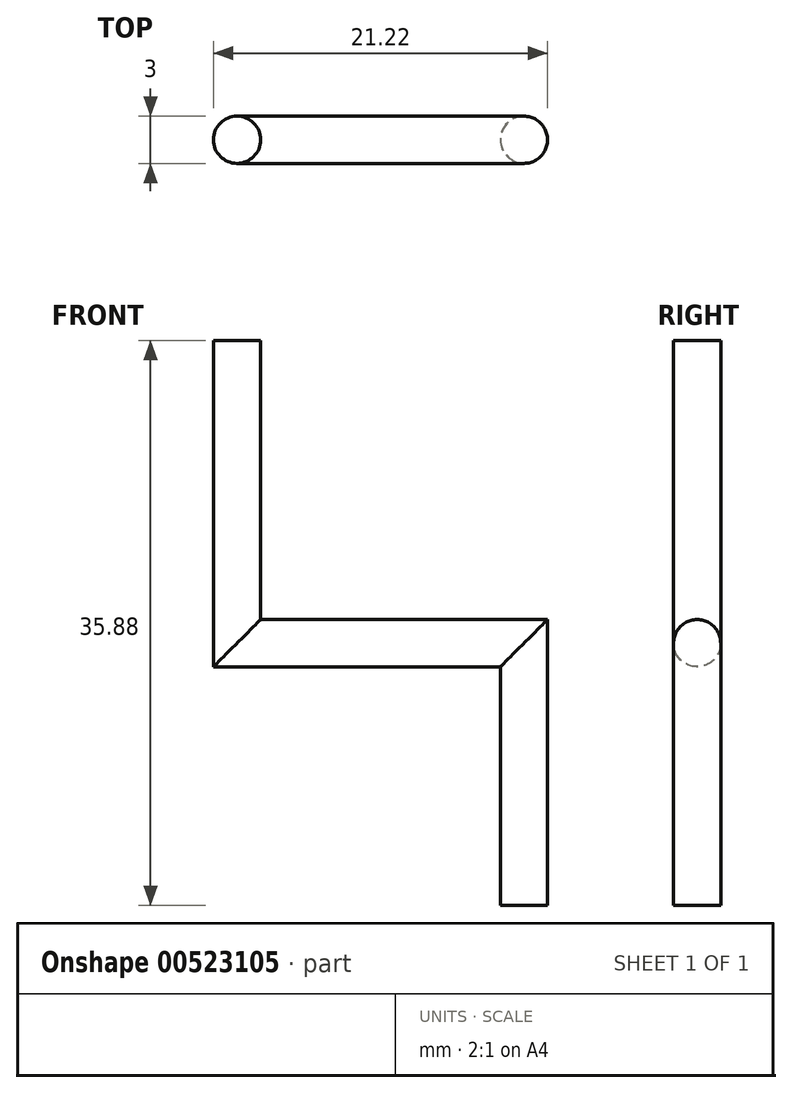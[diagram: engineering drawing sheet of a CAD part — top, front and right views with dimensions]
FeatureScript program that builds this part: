
annotation { "Feature Type Name" : "Feature", "Feature Type Description" : "" }
export const myFeature = defineFeature(function(context is Context, id is Id, definition is map)
    precondition{}
    {
        {
            var Q0;
            Q0=qCreatedBy(makeId("Top.planeOp"),FACE);
            var sketch = newSketch(context, id + "F0", { "sketchPlane" : qUnion([Q0])});
            skCircle(sketch, "E0", {"center": v(0, 0) * mm, "radius": 1.5 * mm});
            skSolve(sketch);
        }
        {
            var Q0;
            Q0=qCreatedBy(makeId("Front.planeOp"),FACE);
            var sketch = newSketch(context, id + "F1", { "sketchPlane" : qUnion([Q0])});
            skLineSegment(sketch, "E1", {"start": v(0, 0) * mm, "end": v(0, 16.66) * mm});
            skLineSegment(sketch, "E2", {"start": v(0, 16.66) * mm, "end": v(-18.22, 16.66) * mm});
            skLineSegment(sketch, "E3", {"start": v(-18.22, 16.66) * mm, "end": v(-18.22, 35.88) * mm});
            skSolve(sketch);
        }
        {
            var Q0;
            Q0=makeQuery(id+"F0.imprint","IMPRINT",FACE,{"disambiguationData":[TD([[makeQuery(id+"F0.imprint","IMPRINT",EDGE,{"derivedFrom":sQuery(id+"F0.wireOp",EDGE,"E0")}),1.0]])]});
            var Q1;
            Q1=sQuery(id+"F1.wireOp",EDGE,"E1");
            var Q2;
            Q2=sQuery(id+"F1.wireOp",EDGE,"E2");
            var Q3;
            Q3=sQuery(id+"F1.wireOp",EDGE,"E3");
            sweep(context, id + "F2", {"profiles" : qUnion([Q0]), "path" : qUnion([Q1, Q2, Q3])});
        }
    });
